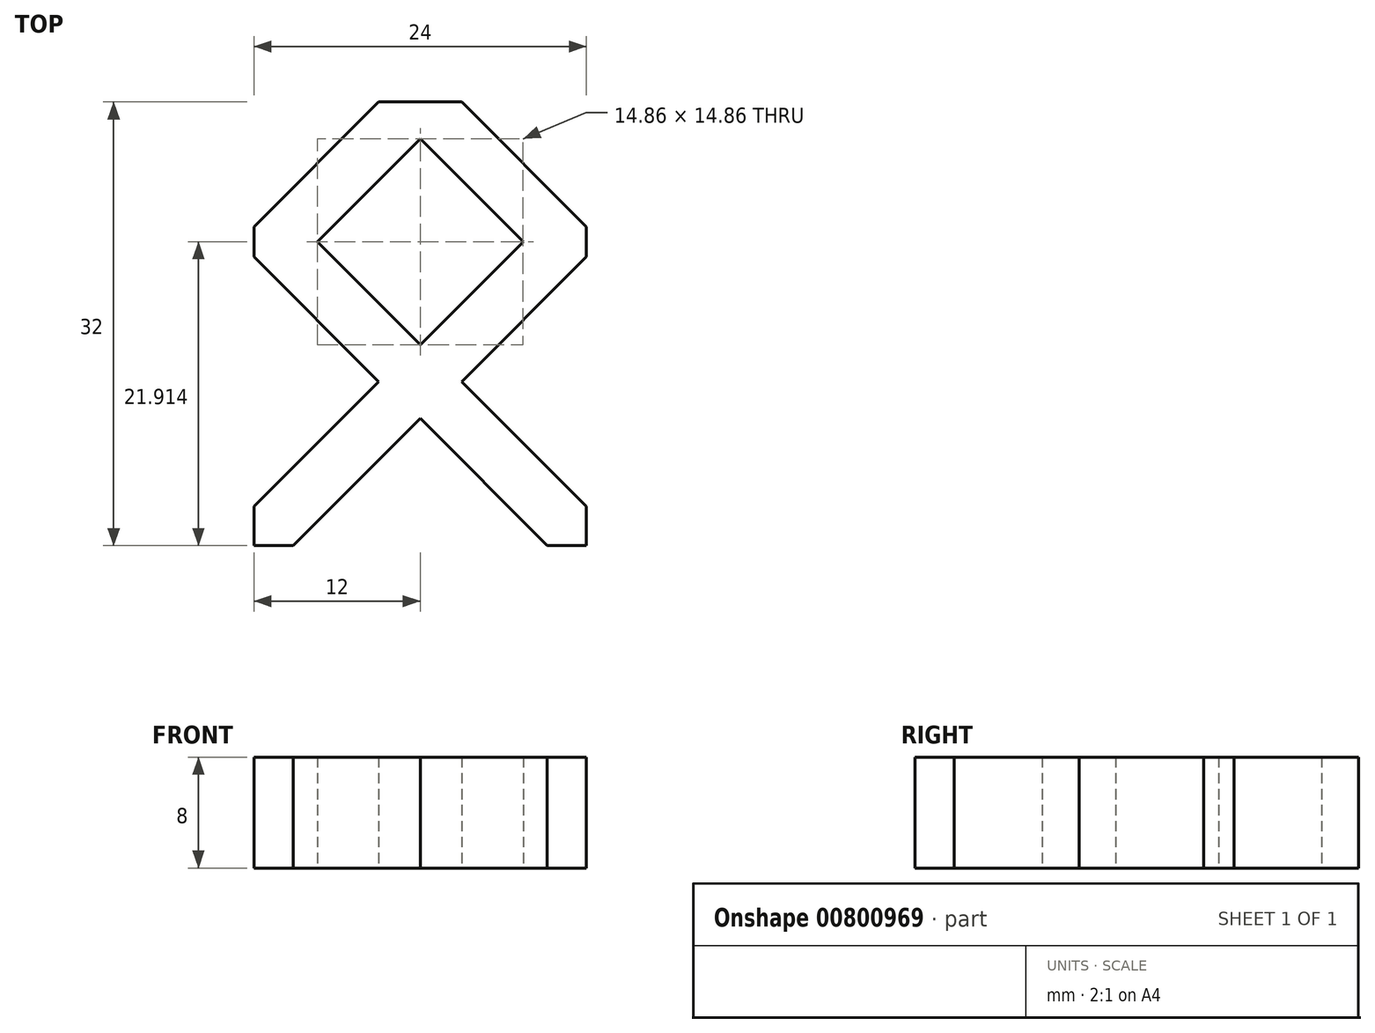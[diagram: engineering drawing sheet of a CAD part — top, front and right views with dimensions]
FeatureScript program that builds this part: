
annotation { "Feature Type Name" : "Feature", "Feature Type Description" : "" }
export const myFeature = defineFeature(function(context is Context, id is Id, definition is map)
    precondition{}
    {
        {
            var Q0;
            Q0=qCreatedBy(makeId("Top.planeOp"),FACE);
            var sketch = newSketch(context, id + "F0", { "sketchPlane" : qUnion([Q0])});
            skLineSegment(sketch, "E0", {"start": v(9, 0) * mm, "end": v(0, -9) * mm});
            skLineSegment(sketch, "E1", {"start": v(0, -9) * mm, "end": v(0, -11.17) * mm});
            skLineSegment(sketch, "E2", {"start": v(0, -11.17) * mm, "end": v(9, -20.17) * mm});
            skLineSegment(sketch, "E3", {"start": v(9, -20.17) * mm, "end": v(0, -29.17) * mm});
            skLineSegment(sketch, "E4", {"start": v(0, -29.17) * mm, "end": v(0, -32) * mm});
            skLineSegment(sketch, "E5", {"start": v(0, -32) * mm, "end": v(2.83, -32) * mm});
            skLineSegment(sketch, "E6", {"start": v(2.83, -32) * mm, "end": v(12, -22.83) * mm});
            skLineSegment(sketch, "E7", {"start": v(12, -22.83) * mm, "end": v(21.17, -32) * mm});
            skPoint(sketch, "E7.endSnap0", {"position": v(1.41, -32) * mm});
            skLineSegment(sketch, "E8", {"start": v(21.17, -32) * mm, "end": v(24, -32) * mm});
            skLineSegment(sketch, "E9", {"start": v(24, -32) * mm, "end": v(24, -29.17) * mm});
            skLineSegment(sketch, "E10", {"start": v(24, -29.17) * mm, "end": v(15, -20.17) * mm});
            skLineSegment(sketch, "E11", {"start": v(15, -20.17) * mm, "end": v(24, -11.17) * mm});
            skLineSegment(sketch, "E12", {"start": v(24, -11.17) * mm, "end": v(24, -9) * mm});
            skLineSegment(sketch, "E13", {"start": v(24, -9) * mm, "end": v(15, 0) * mm});
            skLineSegment(sketch, "E14", {"start": v(15, 0) * mm, "end": v(9, 0) * mm});
            skLineSegment(sketch, "E15", {"start": v(0, -9) * mm, "end": v(24, -9) * mm, "construction": true});
            skLineSegment(sketch, "E16", {"start": v(9, -20.17) * mm, "end": v(9, 0) * mm, "construction": true});
            skLineSegment(sketch, "E17", {"start": v(12, -17.51) * mm, "end": v(4.57, -10.09) * mm});
            skLineSegment(sketch, "E18", {"start": v(4.57, -10.09) * mm, "end": v(12, -2.66) * mm});
            skLineSegment(sketch, "E19", {"start": v(12, -2.66) * mm, "end": v(19.43, -10.09) * mm});
            skLineSegment(sketch, "E20", {"start": v(19.43, -10.09) * mm, "end": v(12, -17.51) * mm});
            skSolve(sketch);
        }
        {
            var Q0;
            Q0=makeQuery(id+"F0.imprint","IMPRINT",FACE,{"disambiguationData":[TD([[makeQuery(id+"F0.imprint","IMPRINT",EDGE,{"derivedFrom":sQuery(id+"F0.wireOp",EDGE,"E0")}),1.0]])]});
            extrude(context, id + "F1", {"entities" : qUnion([Q0]), "depth" : 8 * mm, "offsetDistance" : 25 * mm});
        }
    });
